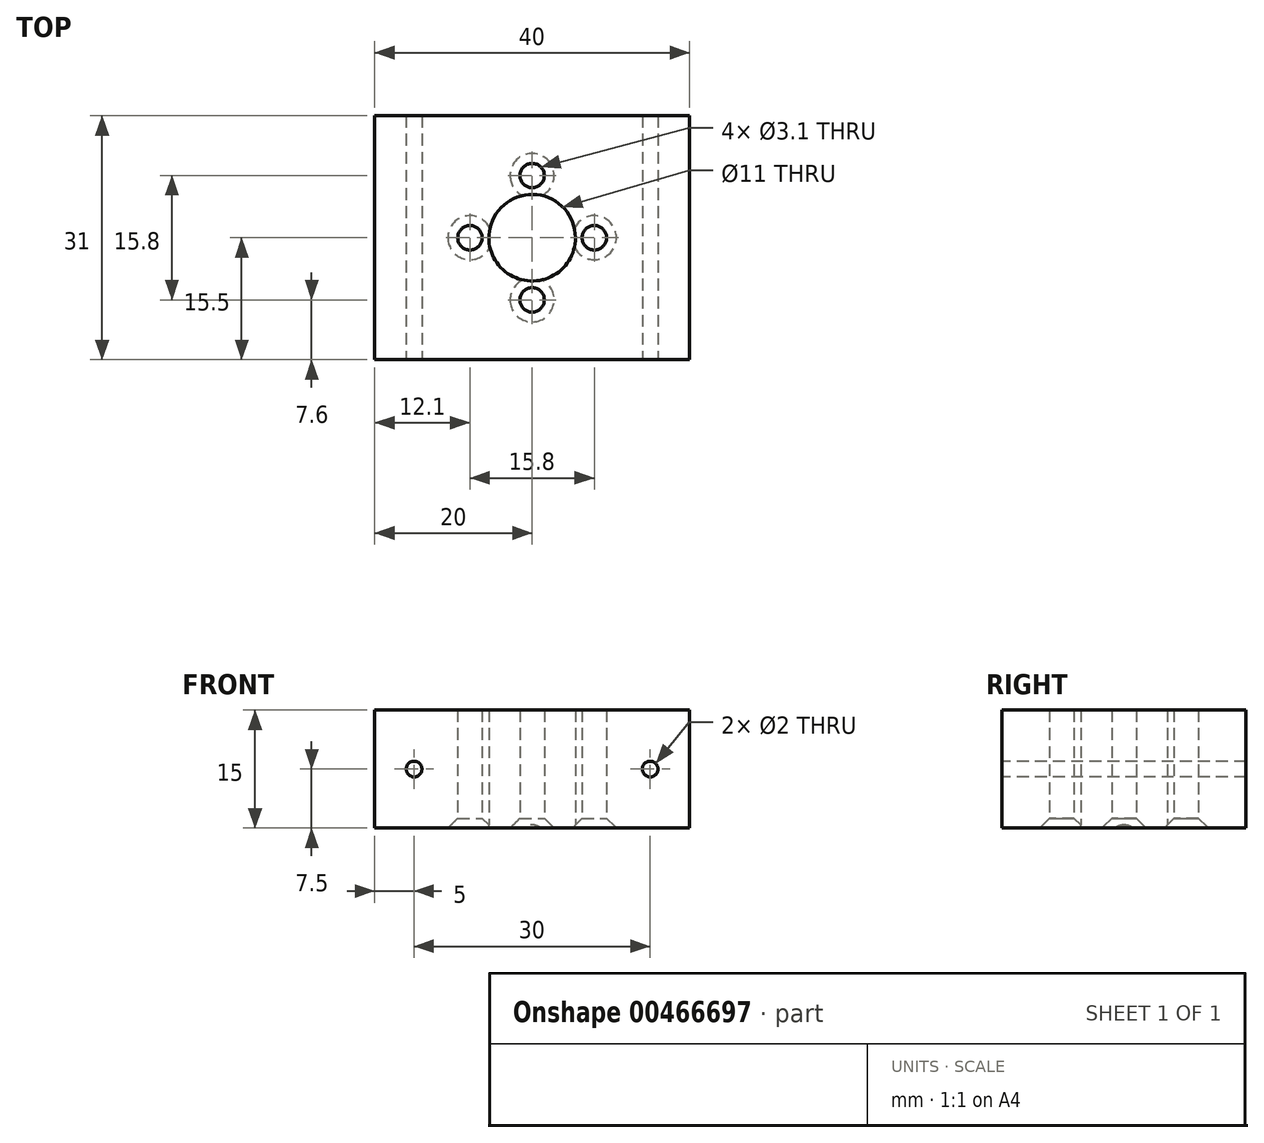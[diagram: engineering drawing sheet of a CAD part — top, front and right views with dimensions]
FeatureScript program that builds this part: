
annotation { "Feature Type Name" : "Feature", "Feature Type Description" : "" }
export const myFeature = defineFeature(function(context is Context, id is Id, definition is map)
    precondition{}
    {
        {
            var Q0;
            Q0=qCreatedBy(makeId("Top.planeOp"),FACE);
            var sketch = newSketch(context, id + "F0", { "sketchPlane" : qUnion([Q0])});
            skLineSegment(sketch, "E0.bottom", {"start": v(20, 15.5) * mm, "end": v(-20, 15.5) * mm});
            skLineSegment(sketch, "E0.top", {"start": v(20, -15.5) * mm, "end": v(-20, -15.5) * mm});
            skLineSegment(sketch, "E0.left", {"start": v(20, 15.5) * mm, "end": v(20, -15.5) * mm});
            skLineSegment(sketch, "E0.right", {"start": v(-20, 15.5) * mm, "end": v(-20, -15.5) * mm});
            skPoint(sketch, "E0.middle", {"position": v(0, 0) * mm});
            skPoint(sketch, "E1", {"position": v(7.9, 0) * mm});
            skPoint(sketch, "E2", {"position": v(0, 7.9) * mm});
            skPoint(sketch, "E3", {"position": v(-7.9, 0) * mm});
            skPoint(sketch, "E4", {"position": v(0, -7.9) * mm});
            skSolve(sketch);
        }
        {
            var Q0;
            Q0=makeQuery(id+"F0.imprint","IMPRINT",FACE,{"disambiguationData":[TD([[makeQuery(id+"F0.imprint","IMPRINT",EDGE,{"derivedFrom":sQuery(id+"F0.wireOp",EDGE,"E0.bottom")}),1.0]])]});
            extrude(context, id + "F1", {"entities" : qUnion([Q0]), "depth" : 15 * mm});
        }
        {
            var Q0;
            Q0=sQuery(id+"F0.wireOp",VERTEX,"E0.middle");
            var Q1;
            Q1=makeQuery(id+"F1.opExtrude","SWEPT_BODY",BODY,{"disambiguationData":[OSD([sQuery(id+"F0.wireOp",EDGE,"E0.bottom"),sQuery(id+"F0.wireOp",EDGE,"E0.top"),sQuery(id+"F0.wireOp",EDGE,"E0.left"),sQuery(id+"F0.wireOp",EDGE,"E0.right")])]});
            hole(context, id + "F2", {"style" : HoleStyle.SIMPLE, "endStyle" : HoleEndStyle.THROUGH, "oppositeDirection" : true, "holeDiameter" : 11 * mm, "isTappedThrough" : true, "tappedDepth" : 12 * mm, "tapClearance" : 3, "locations" : qUnion([Q0]), "scope" : qUnion([Q1])});
        }
        {
            var Q0;
            Q0=sQuery(id+"F0.wireOp",VERTEX,"E1");
            var Q1;
            Q1=sQuery(id+"F0.wireOp",VERTEX,"E2");
            var Q2;
            Q2=sQuery(id+"F0.wireOp",VERTEX,"E3");
            var Q3;
            Q3=sQuery(id+"F0.wireOp",VERTEX,"E4");
            var Q4;
            Q4=makeQuery(id+"F1.opExtrude","SWEPT_BODY",BODY,{"disambiguationData":[OSD([sQuery(id+"F0.wireOp",EDGE,"E0.bottom"),sQuery(id+"F0.wireOp",EDGE,"E0.top"),sQuery(id+"F0.wireOp",EDGE,"E0.left"),sQuery(id+"F0.wireOp",EDGE,"E0.right")])]});
            hole(context, id + "F3", {"style" : HoleStyle.C_SINK, "endStyle" : HoleEndStyle.THROUGH, "oppositeDirection" : true, "holeDiameter" : 3.1 * mm, "cSinkDiameter" : 5.6 * mm, "cSinkAngle" : 90 * degree, "isTappedThrough" : true, "tappedDepth" : 12 * mm, "tapClearance" : 3, "locations" : qUnion([Q0, Q1, Q2, Q3]), "scope" : qUnion([Q4])});
        }
        {
            var Q0;
            Q0=makeQuery(id+"F1.opExtrude","SWEPT_FACE",FACE,{"disambiguationData":[OSD([sQuery(id+"F0.wireOp",EDGE,"E0.top")])]});
            var sketch = newSketch(context, id + "F4", { "sketchPlane" : qUnion([Q0])});
            skPoint(sketch, "E5", {"position": v(-15, 7.5) * mm});
            skPoint(sketch, "E5.positionSnap0", {"position": v(-20, 7.5) * mm});
            skPoint(sketch, "E6", {"position": v(15, 7.5) * mm});
            skSolve(sketch);
        }
        {
            var Q0;
            Q0=sQuery(id+"F4.wireOp",VERTEX,"E5");
            var Q1;
            Q1=sQuery(id+"F4.wireOp",VERTEX,"E6");
            var Q2;
            Q2=makeQuery(id+"F1.opExtrude","SWEPT_BODY",BODY,{"disambiguationData":[OSD([sQuery(id+"F0.wireOp",EDGE,"E0.bottom"),sQuery(id+"F0.wireOp",EDGE,"E0.top"),sQuery(id+"F0.wireOp",EDGE,"E0.left"),sQuery(id+"F0.wireOp",EDGE,"E0.right")])]});
            hole(context, id + "F5", {"style" : HoleStyle.SIMPLE, "endStyle" : HoleEndStyle.THROUGH, "holeDiameter" : 2 * mm, "isTappedThrough" : true, "tappedDepth" : 12 * mm, "tapClearance" : 3, "locations" : qUnion([Q0, Q1]), "scope" : qUnion([Q2])});
        }
    });
